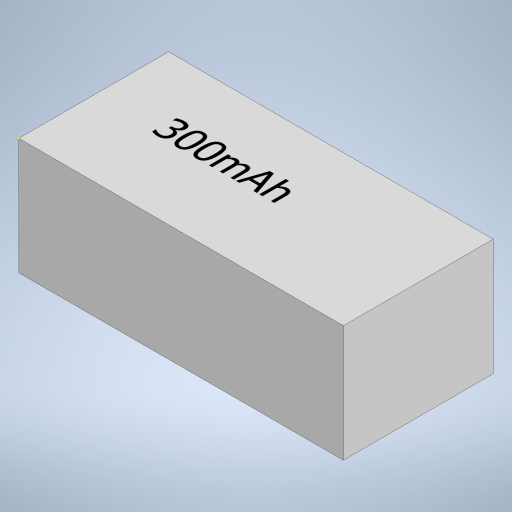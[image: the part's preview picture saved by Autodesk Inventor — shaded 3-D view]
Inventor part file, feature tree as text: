
AUTODESK INVENTOR PART (.ipt)
format: ipt  version: 2023.5 (Build 275446000, 446)  size: 179,200 bytes
history: native  units: mm
features: sketch x2, other x1, extrude x1
ambient origin geometry x8: Origin, YZ Plane, XZ Plane, XY Plane, X Axis, Y Axis, Z Axis, Center Point
bodies: Body1 (feature_tree)
feature tree (4):
  other  "Bryła1"
  extrude  "Wyciągnięcie proste1"  Depth=39.0mm
  sketch  "Szkic2"
  sketch  "Szkic1"
